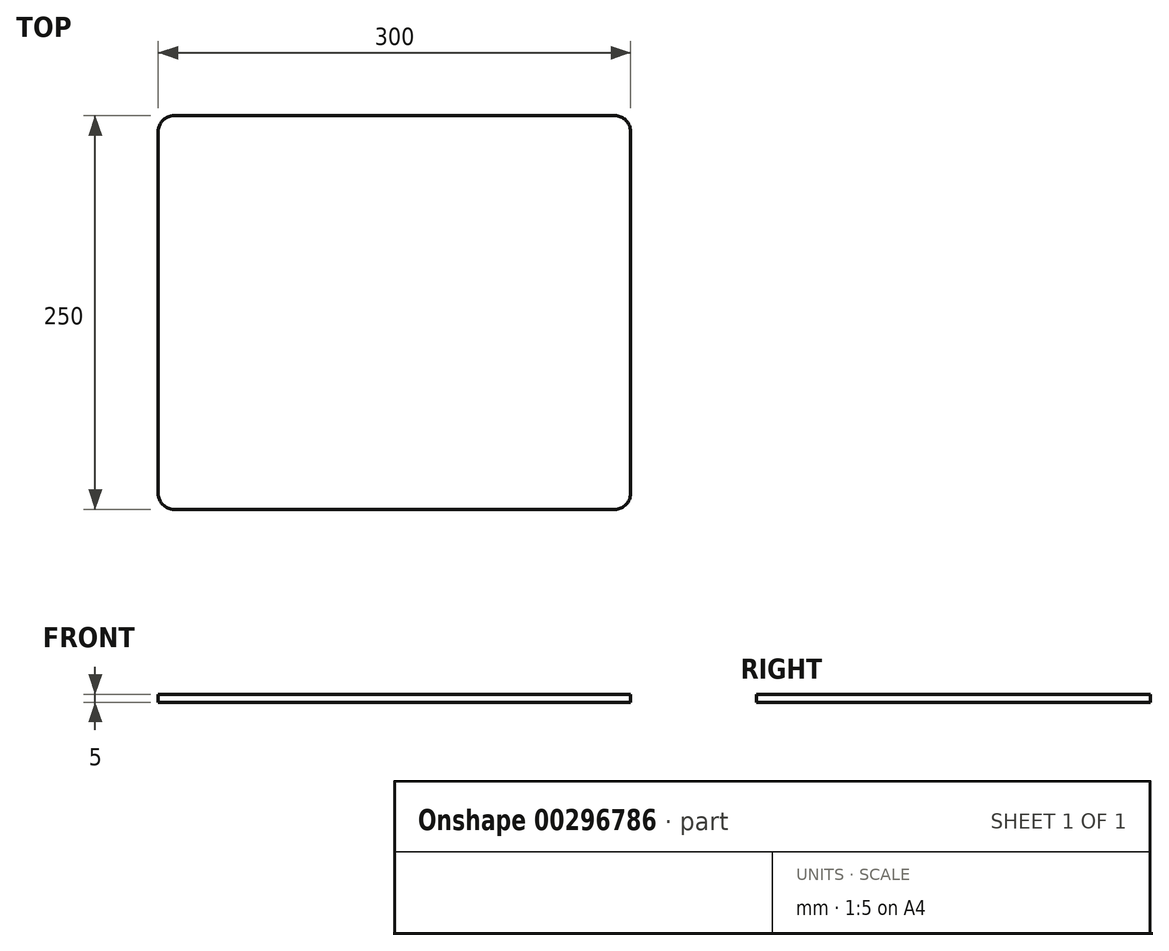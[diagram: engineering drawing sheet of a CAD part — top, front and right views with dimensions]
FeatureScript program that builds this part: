
annotation { "Feature Type Name" : "Feature", "Feature Type Description" : "" }
export const myFeature = defineFeature(function(context is Context, id is Id, definition is map)
    precondition{}
    {
        {
            var Q0;
            Q0=qCreatedBy(makeId("Top.planeOp"),FACE);
            var sketch = newSketch(context, id + "F0", { "sketchPlane" : qUnion([Q0])});
            skLineSegment(sketch, "E0.bottom", {"start": v(-201.83, 100.62) * mm, "end": v(78.17, 100.62) * mm});
            skLineSegment(sketch, "E0.top", {"start": v(-201.83, -149.38) * mm, "end": v(78.17, -149.38) * mm});
            skLineSegment(sketch, "E0.left", {"start": v(-211.83, 90.62) * mm, "end": v(-211.83, -139.38) * mm});
            skLineSegment(sketch, "E0.right", {"start": v(88.17, 90.62) * mm, "end": v(88.17, -139.38) * mm});
            skPoint(sketch, "E1.visualSharp", {"position": v(-211.83, 100.62) * mm});
            skArc(sketch, "E1.filletArc", {"start": v(-201.83, 100.62) * mm, "mid": v(-208.9, 97.69) * mm, "end": v(-211.83, 90.62) * mm});
            skPoint(sketch, "E2.visualSharp", {"position": v(88.17, 100.62) * mm});
            skArc(sketch, "E2.filletArc", {"start": v(88.17, 90.62) * mm, "mid": v(85.24, 97.69) * mm, "end": v(78.17, 100.62) * mm});
            skPoint(sketch, "E3.visualSharp", {"position": v(88.17, -149.38) * mm});
            skArc(sketch, "E3.filletArc", {"start": v(78.17, -149.38) * mm, "mid": v(85.24, -146.45) * mm, "end": v(88.17, -139.38) * mm});
            skPoint(sketch, "E4.visualSharp", {"position": v(-211.83, -149.38) * mm});
            skArc(sketch, "E4.filletArc", {"start": v(-211.83, -139.38) * mm, "mid": v(-208.9, -146.45) * mm, "end": v(-201.83, -149.38) * mm});
            skSolve(sketch);
        }
        {
            var Q0;
            Q0=makeQuery(id+"F0.imprint","IMPRINT",FACE,{"disambiguationData":[TD([[makeQuery(id+"F0.imprint","IMPRINT",EDGE,{"derivedFrom":sQuery(id+"F0.wireOp",EDGE,"E0.bottom")}),-1.0]])]});
            extrude(context, id + "F1", {"entities" : qUnion([Q0]), "depth" : 5 * mm});
        }
    });
